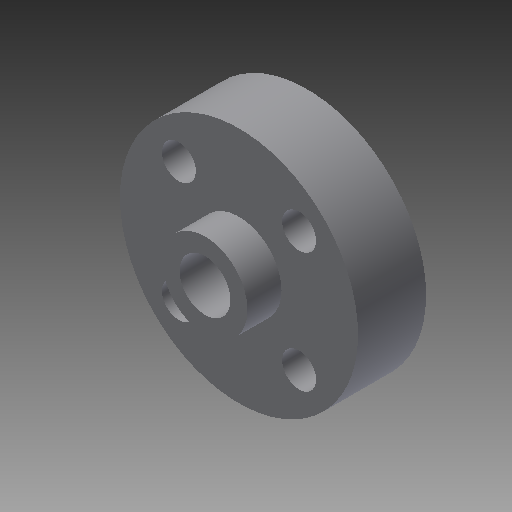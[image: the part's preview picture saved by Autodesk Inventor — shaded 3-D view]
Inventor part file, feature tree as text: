
AUTODESK INVENTOR PART (.ipt)
format: ipt  version: 2017 (Build 210142000, 142)  size: 148,992 bytes
history: native  units: in
note: dims shown in document units (in); Inventor stores cm internally (conversion verified against a paired STEP export)
features: sketch x5, extrude x4, hole x1, pattern_circular x1
ambient origin geometry x8: Origin, YZ Plane, XZ Plane, XY Plane, X Axis, Y Axis, Z Axis, Center Point
bodies: Solid1 (feature_tree)
feature tree (11):
  extrude  "Extrusion1"  Depth=0.1875in
  extrude  "Extrusion2"  Depth=0.125in
  extrude  "Extrusion3"  Depth=0.25in TaperAngle=0.0deg
  hole  "Hole2"  [1 undecoded]
  pattern_circular  "Circular Pattern1"  Count=4 Angle=360.0deg
  extrude  "Extrusion4"  Depth=0.125in
  sketch  "Sketch1"  dims[d0=0.875in d1=0.1875in]
  sketch  "Sketch2"  dims[d2=0.125in d3=0.3125in]
  sketch  "Sketch4"  dims[d4=1.5748in d6=360.0deg d8=0.25in d9=0.0in]
  sketch  "Sketch5"  dims[d10=0.3125in d11=0.125in d12=0.0in d20=1.5748in d22=360.0deg]
  sketch  "Sketch6"  dims[d24=0.25in d25=0.0in d26=0.125in d27=0.3125in d28=0.125in d29=0.75in d30=0.375in d31=0.25in d32=0.5635in d33=1.0in d34=0.8108in d35=3.1496in d36=360.0deg d38=1.5748in d40=360.0deg d42=0.25in d43=0.0in]
note: 1 required parameter value undecoded (feature->parameter linkage not recoverable at this tier; creation-order binding heuristic only, values carry confidence <= 0.55)
